FCSTD DOCUMENT  (FreeCAD 1.0R38642 (Git))
Label: one_of_each_sketch_geometry
License: All rights reserved
LicenseURL: http://en.wikipedia.org/wiki/All_rights_reserved
objects: Sketcher::SketchObject×1, PartDesign::Body×1
note: 3 computed .brp shape members not serialized (recipe doc carries the construction recipe); baked Part::Feature solids carry a one-line shape summary decoded from their .brp

FEATURE [Sketcher::SketchObject] Sketch
  ArcFitTolerance = 1e-06
  AttachmentSupport = -> [XY_Plane]
  FullyConstrained = true
  MakeInternals = false
  MapMode = 5
  sketch-geometry (12):
    g0: LineSegment StartX=0 StartY=0 StartZ=0 EndX=1 EndY=0 EndZ=0
    g1: LineSegment StartX=1 StartY=0 StartZ=0 EndX=1 EndY=1 EndZ=0
    g2: LineSegment StartX=1 StartY=1 StartZ=0 EndX=0 EndY=1 EndZ=0
    g3: LineSegment StartX=0 StartY=1 StartZ=0 EndX=0 EndY=0 EndZ=0
    g4: Circle CenterX=0 CenterY=0 CenterZ=0 NormalX=0 NormalY=0 NormalZ=1 AngleXU=0 Radius=2.5
    g5: Ellipse CenterX=0 CenterY=0 CenterZ=0 NormalX=0 NormalY=0 NormalZ=1 MajorRadius=5 MinorRadius=2.5 AngleXU=0.785398
    g6: LineSegment [constr] StartX=3.53553 StartY=3.53553 StartZ=0 EndX=-3.53553 EndY=-3.53553 EndZ=0
    g7: LineSegment [constr] StartX=-1.76777 StartY=1.76777 StartZ=0 EndX=1.76777 EndY=-1.76777 EndZ=0
    g8: GeomPoint [constr] X=3.06186 Y=3.06186 Z=0
    g9: GeomPoint [constr] X=-3.06186 Y=-3.06186 Z=0
    g10: ArcOfCircle CenterX=0 CenterY=0 CenterZ=0 NormalX=0 NormalY=0 NormalZ=1 AngleXU=0 Radius=5 StartAngle=0 EndAngle=1.5708
    g11: GeomPoint X=5 Y=5 Z=0
  constraints (24):
    c: Coincident(g0,g1)
    c: Coincident(g1,g2)
    c: Coincident(g2,g3)
    c: Coincident(g3,g0)
    c: Horizontal(g0)
    c: Horizontal(g2)
    c: Vertical(g1)
    c: Vertical(g3)
    c: Coincident(g0,g-1)
    c: Equal(g2,g3)
    c: DistanceX(g2,g2) = 1
    c: Coincident(g4,g0)
    c: Diameter(g4) = 5
    c: InternalAlignment(g6-g9 -> g5) x4
    c: Coincident(g5,g0)
    c: Distance(g6,g6) = 10
    c: Distance(g7,g7) = 5
    c: Angle(g-1,g6) = 0.785398
    c: Coincident(g10,g0)
    c: PointOnObject(g10,g-2)
    c: PointOnObject(g10,g-1)
    c: Radius(g10) = 5
    c: DistanceX(g-1,g11) = 5
    c: DistanceY(g-1,g11) = 5
FEATURE [PartDesign::Body] Body
  AllowCompound = false
  Group = -> [Sketch]
  Origin = -> Origin
